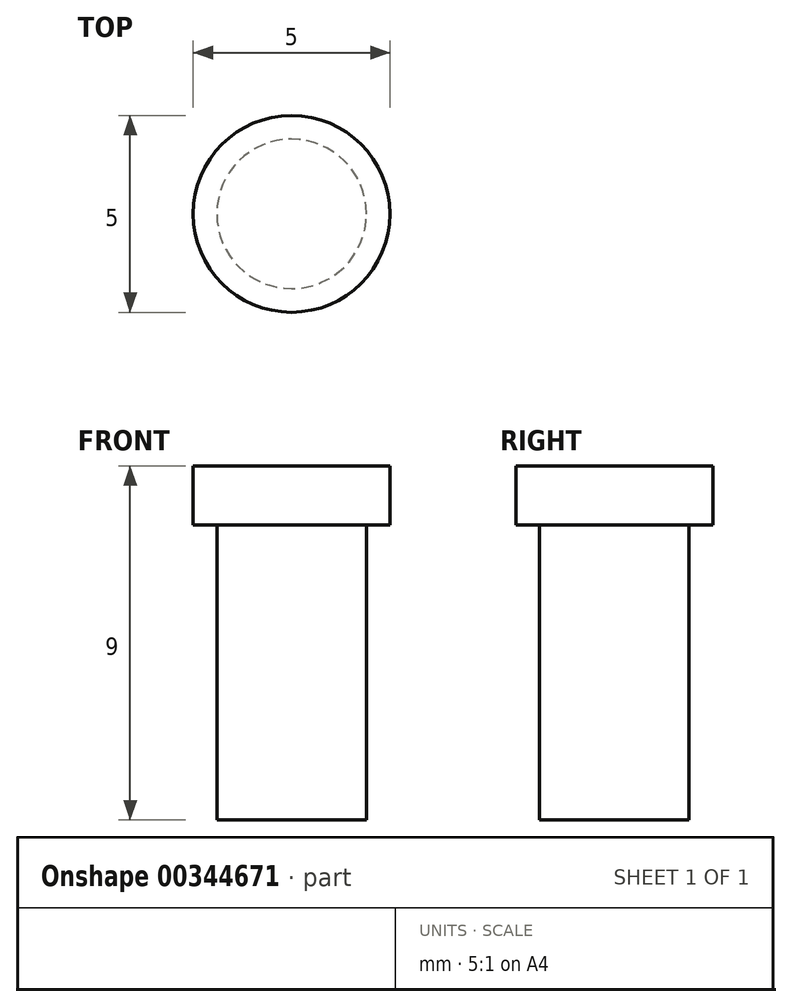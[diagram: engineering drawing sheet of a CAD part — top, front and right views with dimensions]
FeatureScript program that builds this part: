
annotation { "Feature Type Name" : "Feature", "Feature Type Description" : "" }
export const myFeature = defineFeature(function(context is Context, id is Id, definition is map)
    precondition{}
    {
        {
            var Q0;
            Q0=qCreatedBy(makeId("Top.planeOp"),FACE);
            var sketch = newSketch(context, id + "F0", { "sketchPlane" : qUnion([Q0])});
            skCircle(sketch, "E0", {"center": v(0, 0) * mm, "radius": 1.9 * mm});
            skCircle(sketch, "E1", {"center": v(0, 0) * mm, "radius": 2.5 * mm});
            skSolve(sketch);
        }
        {
            var Q0;
            Q0=makeQuery(id+"F0.imprint","IMPRINT",FACE,{"disambiguationData":[TD([[makeQuery(id+"F0.imprint","IMPRINT",EDGE,{"derivedFrom":sQuery(id+"F0.wireOp",EDGE,"E0")}),1.0]])]});
            extrude(context, id + "F1", {"entities" : qUnion([Q0]), "oppositeDirection" : true, "depth" : 7.5 * mm});
        }
        {
            var Q0;
            Q0 = qSketchRegion(id + "F0", true);
            var Q1;
            Q1=makeQuery(id+"F0.imprint","IMPRINT",FACE,{"disambiguationData":[TD([[makeQuery(id+"F0.imprint","IMPRINT",EDGE,{"derivedFrom":sQuery(id+"F0.wireOp",EDGE,"E0")}),1.0]])]});
            extrude(context, id + "F2", {"entities" : qUnion([Q0, Q1]), "operationType" : NewBodyOperationType.ADD, "depth" : 1.5 * mm});
        }
    });
